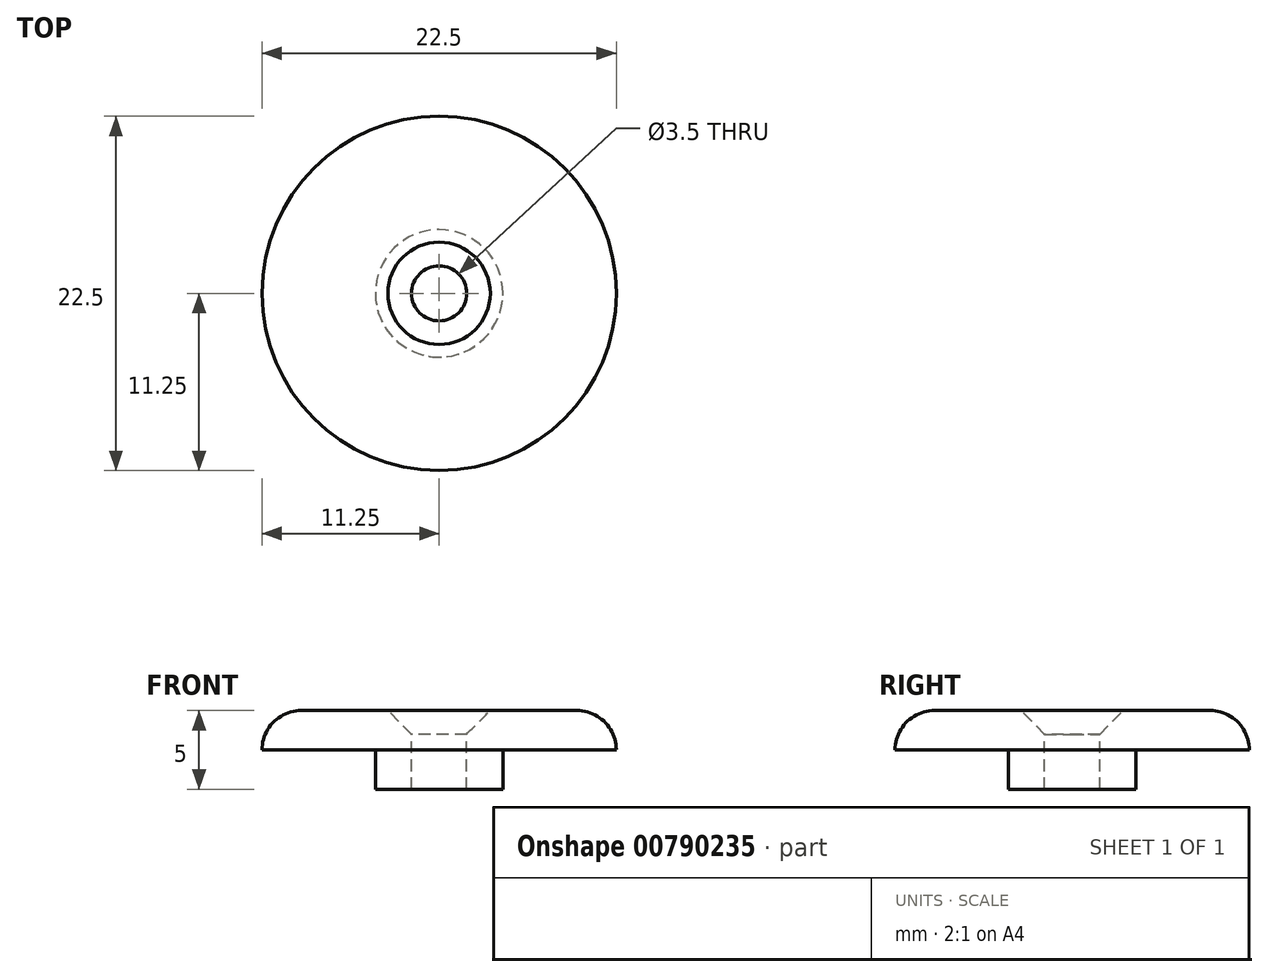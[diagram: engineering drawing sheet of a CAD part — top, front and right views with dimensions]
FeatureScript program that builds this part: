
annotation { "Feature Type Name" : "Feature", "Feature Type Description" : "" }
export const myFeature = defineFeature(function(context is Context, id is Id, definition is map)
    precondition{}
    {
        {
            var Q0;
            Q0=qCreatedBy(makeId("Top.planeOp"),FACE);
            var sketch = newSketch(context, id + "F0", { "sketchPlane" : qUnion([Q0])});
            skCircle(sketch, "E0", {"center": v(0, 0) * mm, "radius": 11.25 * mm});
            skSolve(sketch);
        }
        {
            var Q0;
            Q0 = qSketchRegion(id + "F0", true);
            extrude(context, id + "F1", {"entities" : qUnion([Q0]), "depth" : 2.5 * mm, "offsetDistance" : 25 * mm});
        }
        {
            var Q0;
            Q0=makeQuery(id+"F1.opExtrude","CAP_FACE",FACE,{"disambiguationData":[OSD([sQuery(id+"F0.wireOp",EDGE,"E0")])],"isStart":false});
            fillet(context, id + "F2", {"entities" : qUnion([Q0]), "radius" : 2.5 * mm, "tangentPropagation" : true, "allowEdgeOverflow" : false});
        }
        {
            var Q0;
            Q0=makeQuery(id+"F1.opExtrude","CAP_FACE",FACE,{"disambiguationData":[OSD([sQuery(id+"F0.wireOp",EDGE,"E0")])],"isStart":false});
            var sketch = newSketch(context, id + "F3", { "sketchPlane" : qUnion([Q0])});
            skPoint(sketch, "E1", {"position": v(0, 0) * mm});
            skSolve(sketch);
        }
        {
            var Q0;
            Q0=makeQuery(id+"F1.opExtrude","CAP_FACE",FACE,{"disambiguationData":[OSD([sQuery(id+"F0.wireOp",EDGE,"E0")])],"isStart":true});
            var sketch = newSketch(context, id + "F4", { "sketchPlane" : qUnion([Q0])});
            skCircle(sketch, "E2", {"center": v(0, 0) * mm, "radius": 4.05 * mm});
            skSolve(sketch);
        }
        {
            var Q0;
            Q0 = qSketchRegion(id + "F4", true);
            extrude(context, id + "F5", {"entities" : qUnion([Q0]), "operationType" : NewBodyOperationType.ADD, "depth" : 2.5 * mm, "offsetDistance" : 25 * mm});
        }
        {
            var Q0;
            Q0=sQuery(id+"F3.wireOp",VERTEX,"E1");
            var Q1;
            Q1=makeQuery(id+"F1.opExtrude","SWEPT_BODY",BODY,{"disambiguationData":[OSD([sQuery(id+"F0.wireOp",EDGE,"E0")])]});
            hole(context, id + "F6", {"style" : HoleStyle.C_SINK, "endStyle" : HoleEndStyle.BLIND, "holeDiameter" : 3.5 * mm, "cSinkDiameter" : 6.5 * mm, "cSinkAngle" : 90 * degree, "majorDiameter" : 5 * mm, "holeDepth" : 7 * mm, "isTappedThrough" : true, "tappedDepth" : 12 * mm, "tapClearance" : 3, "startFromSketch" : true, "locations" : qUnion([Q0]), "scope" : qUnion([Q1])});
        }
    });
